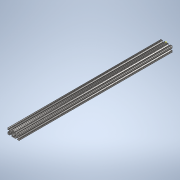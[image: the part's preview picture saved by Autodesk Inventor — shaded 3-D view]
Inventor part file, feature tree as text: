
AUTODESK INVENTOR PART (.ipt)
format: ipt  version: 2020 (Build 240168000, 168)  size: 356,864 bytes
history: native  units: in
note: dims shown in document units (in); Inventor stores cm internally (conversion verified against a paired STEP export)
features: sketch x2, extrude x1
ambient origin geometry x8: Origin, YZ Plane, XZ Plane, XY Plane, X Axis, Y Axis, Z Axis, Center Point
bodies: Solid1 (feature_tree)
feature tree (3):
  extrude  "Extrusion1"  [1 undecoded]
  sketch  "Sketch2"
  sketch  "Sketch1"  dims[d0=26.0in d1=0.0in]
note: 1 required parameter value undecoded (feature->parameter linkage not recoverable at this tier; creation-order binding heuristic only, values carry confidence <= 0.55)
